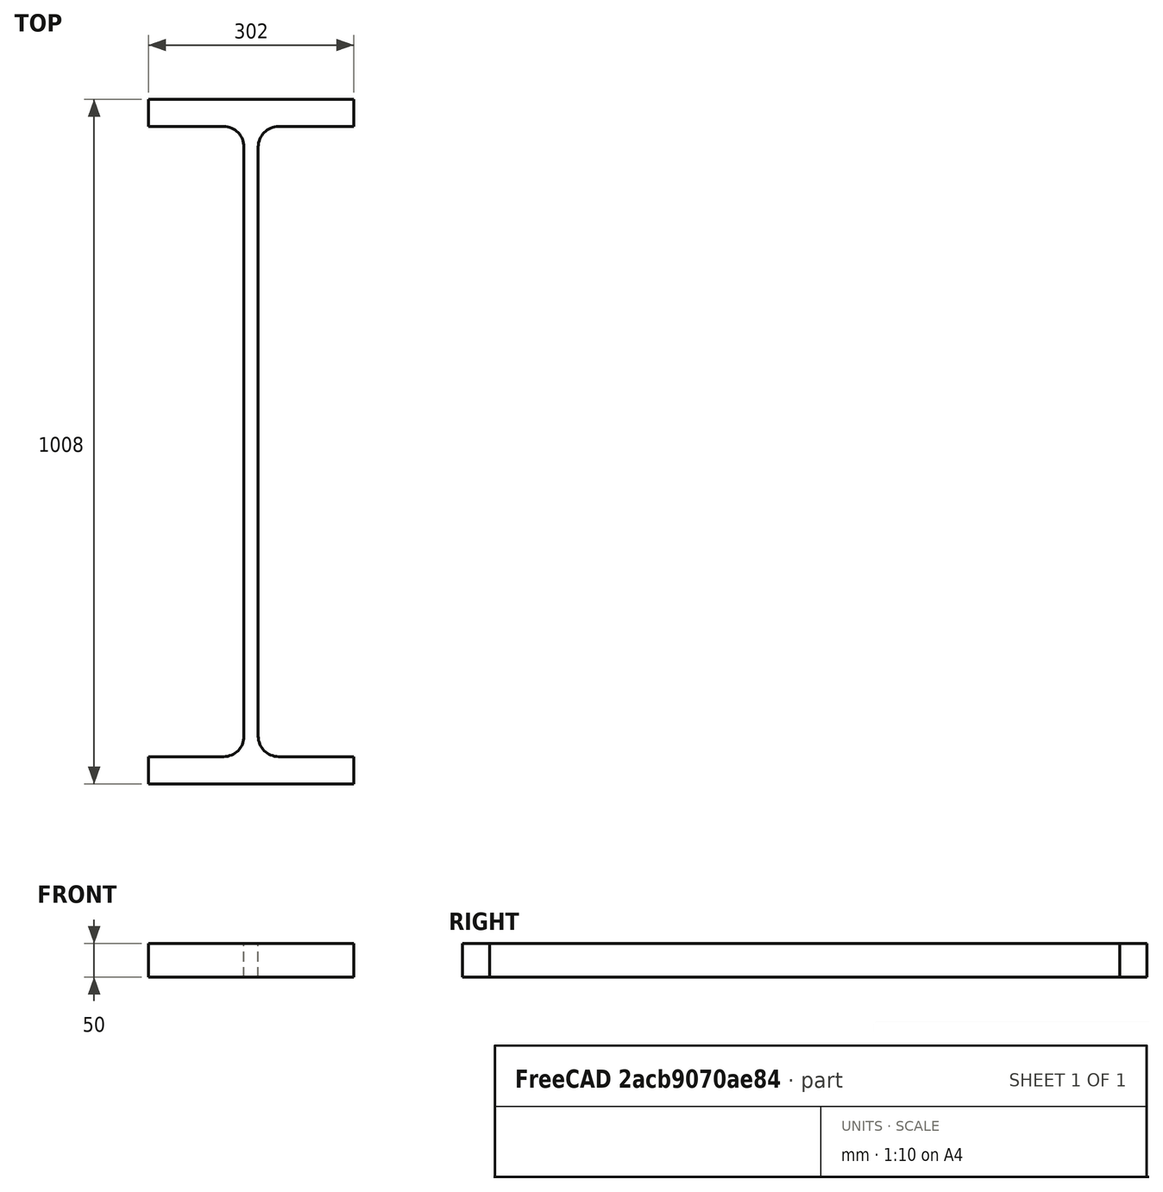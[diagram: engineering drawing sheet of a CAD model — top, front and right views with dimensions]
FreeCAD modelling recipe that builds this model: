
FCSTD DOCUMENT  (FreeCAD 0.15R4671 (Git))
Label: HE-M-Profile 1000 DIN1025-4 S235JR
License: All rights reserved
LicenseURL: http://en.wikipedia.org/wiki/All_rights_reserved
objects: Sketcher::SketchObject×1, Part::Extrusion×1
note: 2 computed .brp shape members not serialized (recipe doc carries the construction recipe); baked Part::Feature solids carry a one-line shape summary decoded from their .brp

FEATURE [Sketcher::SketchObject] Sketch
  sketch-geometry (16):
    g0: LineSegment StartX=10.5 StartY=-434 StartZ=0 EndX=10.5 EndY=434 EndZ=0
    g1: LineSegment StartX=40.5 StartY=464 StartZ=0 EndX=151 EndY=464 EndZ=0
    g2: LineSegment StartX=151 StartY=464 StartZ=0 EndX=151 EndY=504 EndZ=0
    g3: LineSegment StartX=151 StartY=504 StartZ=0 EndX=-151 EndY=504 EndZ=0
    g4: LineSegment StartX=-151 StartY=504 StartZ=0 EndX=-151 EndY=464 EndZ=0
    g5: LineSegment StartX=-151 StartY=464 StartZ=0 EndX=-40.5 EndY=464 EndZ=0
    g6: LineSegment StartX=-10.5 StartY=434 StartZ=0 EndX=-10.5 EndY=-434 EndZ=0
    g7: LineSegment StartX=-40.5 StartY=-464 StartZ=0 EndX=-151 EndY=-464 EndZ=0
    g8: LineSegment StartX=-151 StartY=-464 StartZ=0 EndX=-151 EndY=-504 EndZ=0
    g9: LineSegment StartX=-151 StartY=-504 StartZ=0 EndX=151 EndY=-504 EndZ=0
    g10: LineSegment StartX=151 StartY=-504 StartZ=0 EndX=151 EndY=-464 EndZ=0
    g11: LineSegment StartX=151 StartY=-464 StartZ=0 EndX=40.5 EndY=-464 EndZ=0
    g12: ArcOfCircle CenterX=40.5 CenterY=434 CenterZ=0 NormalX=0 NormalY=0 NormalZ=1 Radius=30 StartAngle=1.5708 EndAngle=3.14159
    g13: ArcOfCircle CenterX=40.5 CenterY=-434 CenterZ=0 NormalX=0 NormalY=0 NormalZ=1 Radius=30 StartAngle=3.14159 EndAngle=4.71239
    g14: ArcOfCircle CenterX=-40.5 CenterY=434 CenterZ=0 NormalX=0 NormalY=0 NormalZ=1 Radius=30 StartAngle=0 EndAngle=1.5708
    g15: ArcOfCircle CenterX=-40.5 CenterY=-434 CenterZ=0 NormalX=0 NormalY=0 NormalZ=1 Radius=30 StartAngle=4.71239 EndAngle=6.28319
  constraints (42):
    c: Vertical(g0)
    c: Coincident(g2,g1)
    c: Vertical(g2)
    c: Coincident(g3,g2)
    c: Coincident(g4,g3)
    c: Vertical(g4)
    c: Coincident(g5,g4)
    c: Horizontal(g5)
    c: Vertical(g6)
    c: Horizontal(g7)
    c: Coincident(g8,g7)
    c: Vertical(g8)
    c: Coincident(g9,g8)
    c: Horizontal(g9)
    c: Coincident(g10,g9)
    c: Vertical(g10)
    c: Coincident(g11,g10)
    c: Horizontal(g11)
    c: Tangent(g1,g12) = 1.5708
    c: Tangent(g0,g12) = 1.5708
    c: Tangent(g0,g13) = 1.5708
    c: Tangent(g11,g13) = 1.5708
    c: Tangent(g5,g14) = 1.5708
    c: Tangent(g6,g14) = 1.5708
    c: Tangent(g6,g15) = 1.5708
    c: Tangent(g7,g15) = 1.5708
    c: Equal(g3,g9)
    c: Equal(g2,g4)
    c: Equal(g4,g8)
    c: Equal(g8,g10)
    c: Equal(g12,g14)
    c: Equal(g14,g15)
    c: Equal(g15,g13)
    c: Symmetric(g2,g3,g-2)
    c: Symmetric(g9,g8,g-2)
    c: Symmetric(g0,g6,g-2)
    c: Symmetric(g2,g9,g-1)
    c: DistanceY(g2,g9) = -1008
    c: DistanceX(g3) = -302
    c: DistanceX(g0,g6) = -21
    c: DistanceY(g2) = 40
    c: Radius(g12) = 30
FEATURE [Part::Extrusion] Extrude  label="HE-M-Profile 1000 DIN1025-4 S235JR"
  Base = -> Sketch
  Dir = (0,0,50)
  Solid = true
